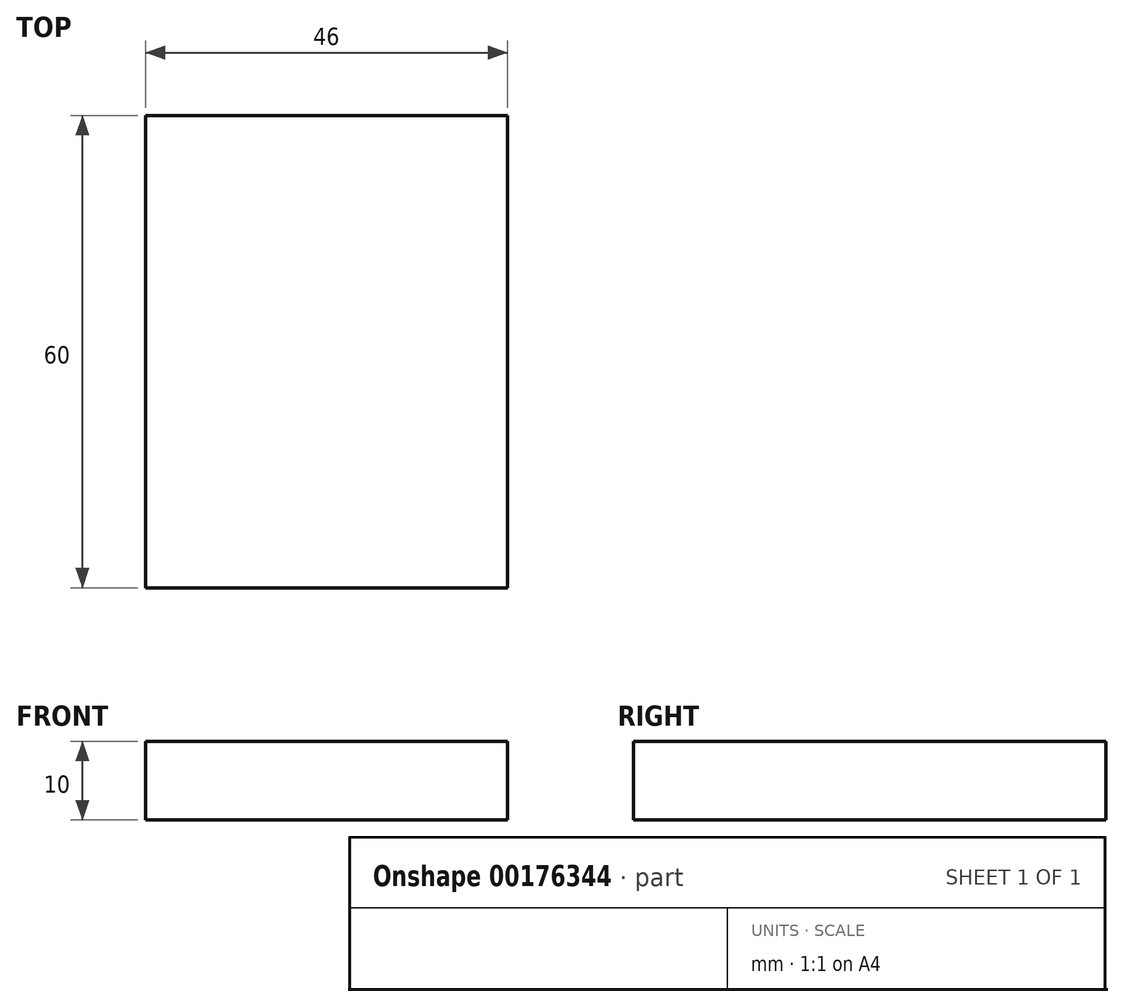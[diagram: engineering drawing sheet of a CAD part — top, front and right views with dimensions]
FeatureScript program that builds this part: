
annotation { "Feature Type Name" : "Feature", "Feature Type Description" : "" }
export const myFeature = defineFeature(function(context is Context, id is Id, definition is map)
    precondition{}
    {
        {
            var Q0;
            Q0=qCreatedBy(makeId("Top.planeOp"),FACE);
            var sketch = newSketch(context, id + "F0", { "sketchPlane" : qUnion([Q0])});
            skLineSegment(sketch, "E0.bottom", {"start": v(-23, -30) * mm, "end": v(23, -30) * mm});
            skLineSegment(sketch, "E0.top", {"start": v(-23, 30) * mm, "end": v(23, 30) * mm});
            skLineSegment(sketch, "E0.left", {"start": v(-23, -30) * mm, "end": v(-23, 30) * mm});
            skLineSegment(sketch, "E0.right", {"start": v(23, -30) * mm, "end": v(23, 30) * mm});
            skSolve(sketch);
        }
        {
            var Q0;
            Q0 = qSketchRegion(id + "F0", true);
            extrude(context, id + "F1", {"entities" : qUnion([Q0]), "depth" : 10 * mm});
        }
    });
